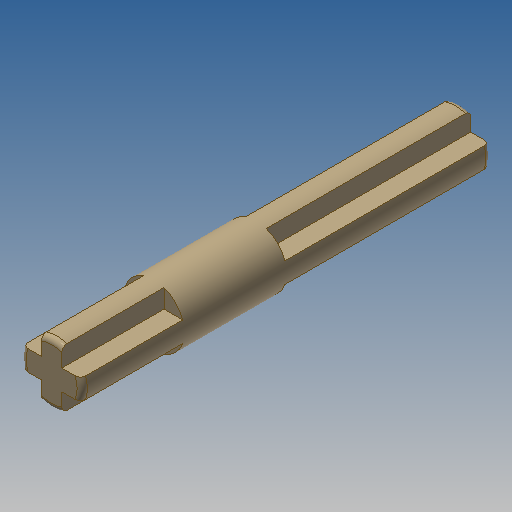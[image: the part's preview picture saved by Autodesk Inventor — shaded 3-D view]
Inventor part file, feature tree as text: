
AUTODESK INVENTOR PART (.ipt)
format: ipt  version: 2022.2 (Build 262287000, 287)  size: 172,032 bytes
history: native  units: in
note: dims shown in document units (in); Inventor stores cm internally (conversion verified against a paired STEP export)
features: extrude x3, sketch x3, fillet x1
ambient origin geometry x8: Origin, YZ Plane, XZ Plane, XY Plane, X Axis, Y Axis, Z Axis, Center Point
bodies: Solid1 (feature_tree)
feature tree (7):
  extrude  "Extrusion1"  Depth=0.315in
  extrude  "Extrusion2"  Depth=0.063in
  extrude  "Extrusion3"  TaperAngle=0.0deg  [1 undecoded]
  fillet  "Fillet1"  Radius=0.063in
  sketch  "Sketch1"  dims[d0=0.189in d1=0.315in]
  sketch  "Sketch2"  dims[d2=0.0in d4=0.063in]
  sketch  "Sketch3"  dims[d5=0.315in d6=0.0in d7=0.063in d8=0.6299in d9=0.0in d11=0.0157in]
note: 1 required parameter value undecoded (feature->parameter linkage not recoverable at this tier; creation-order binding heuristic only, values carry confidence <= 0.55)
